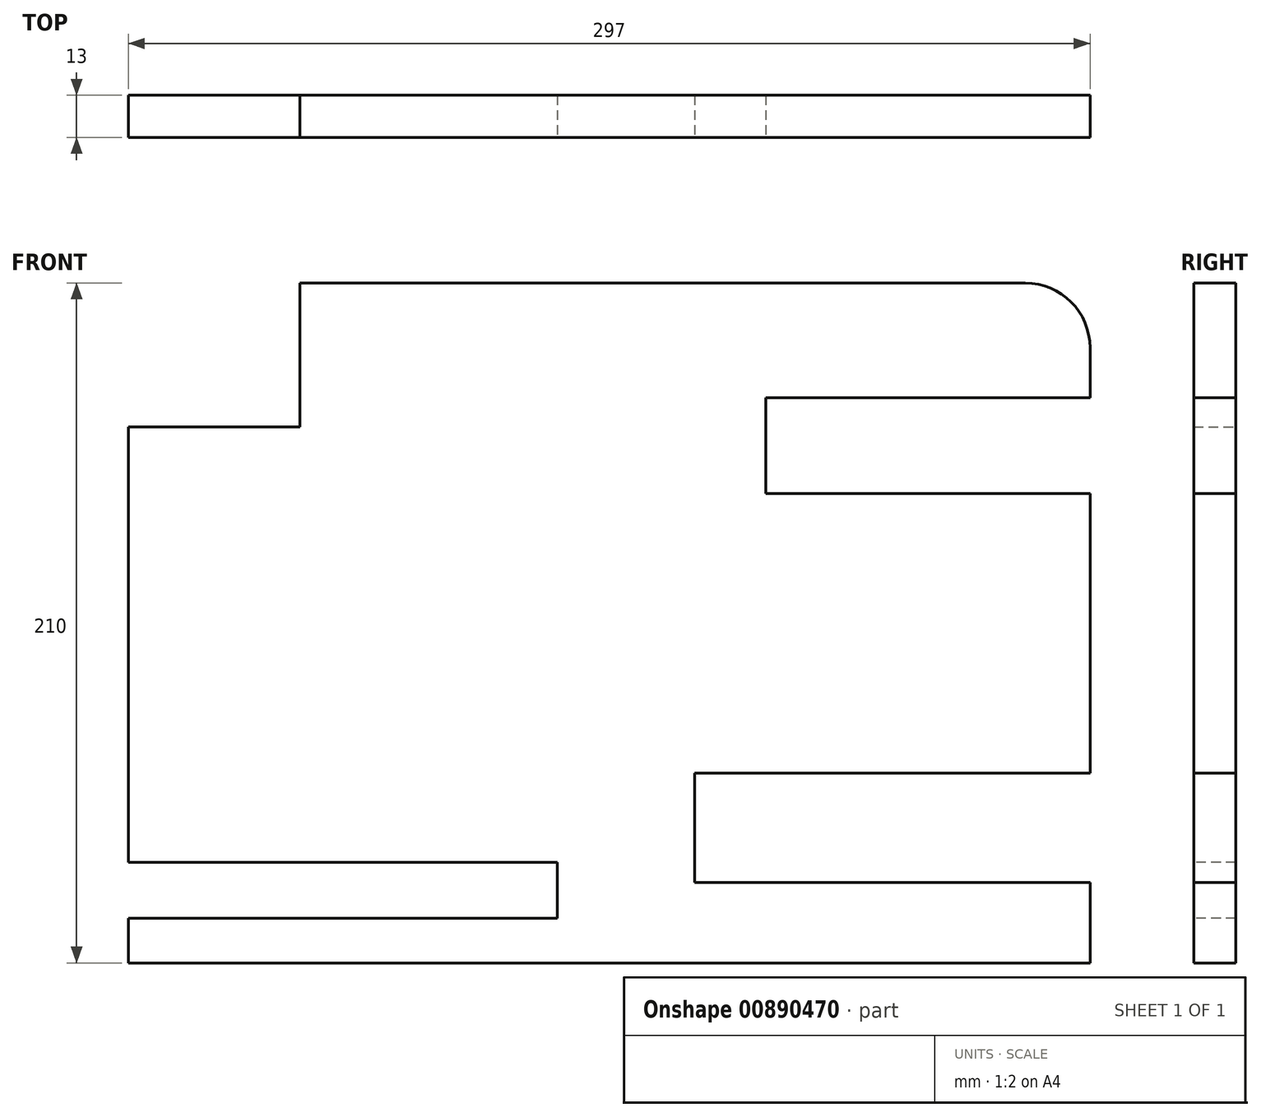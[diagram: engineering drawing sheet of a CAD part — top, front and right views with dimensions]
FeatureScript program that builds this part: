
annotation { "Feature Type Name" : "Feature", "Feature Type Description" : "" }
export const myFeature = defineFeature(function(context is Context, id is Id, definition is map)
    precondition{}
    {
        {
            var Q0;
            Q0=qCreatedBy(makeId("Front.planeOp"),FACE);
            var sketch = newSketch(context, id + "F0", { "sketchPlane" : qUnion([Q0])});
            skLineSegment(sketch, "E0.bottom", {"start": v(-79.44, 101.56) * mm, "end": v(144.58, 101.56) * mm});
            skLineSegment(sketch, "E0.top", {"start": v(-132.42, -108.44) * mm, "end": v(164.58, -108.44) * mm});
            skLineSegment(sketch, "E0.left", {"start": v(-132.42, 57.16) * mm, "end": v(-132.42, -108.44) * mm});
            skLineSegment(sketch, "E0.right", {"start": v(164.58, 81.56) * mm, "end": v(164.58, -108.44) * mm});
            skPoint(sketch, "E1.visualSharp", {"position": v(164.58, 101.56) * mm});
            skArc(sketch, "E1.filletArc", {"start": v(164.58, 81.56) * mm, "mid": v(158.73, 95.7) * mm, "end": v(144.58, 101.56) * mm});
            skLineSegment(sketch, "E2", {"start": v(-79.44, 101.56) * mm, "end": v(-79.44, 57.16) * mm});
            skLineSegment(sketch, "E3", {"start": v(-79.44, 57.16) * mm, "end": v(-132.42, 57.16) * mm});
            skPoint(sketch, "E4.orphan", {"position": v(-132.42, 101.56) * mm});
            skSolve(sketch);
        }
        {
            var Q0;
            Q0 = qSketchRegion(id + "F0", true);
            extrude(context, id + "F1", {"entities" : qUnion([Q0]), "depth" : 13 * mm, "offsetDistance" : 25 * mm});
        }
        {
            var Q0;
            Q0=makeQuery(id+"F1.opExtrude","CAP_FACE",FACE,{"disambiguationData":[OSD([sQuery(id+"F0.wireOp",EDGE,"E0.bottom"),sQuery(id+"F0.wireOp",EDGE,"E0.top"),sQuery(id+"F0.wireOp",EDGE,"E0.left"),sQuery(id+"F0.wireOp",EDGE,"E0.right"),sQuery(id+"F0.wireOp",EDGE,"E1.filletArc"),sQuery(id+"F0.wireOp",EDGE,"E2"),sQuery(id+"F0.wireOp",EDGE,"E3")])],"isStart":false});
            var sketch = newSketch(context, id + "F2", { "sketchPlane" : qUnion([Q0])});
            skLineSegment(sketch, "E5.bottom", {"start": v(-132.42, -77.33) * mm, "end": v(0, -77.33) * mm});
            skLineSegment(sketch, "E5.top", {"start": v(-132.42, -94.6) * mm, "end": v(0, -94.6) * mm});
            skLineSegment(sketch, "E5.left", {"start": v(-132.42, -77.33) * mm, "end": v(-132.42, -94.6) * mm});
            skLineSegment(sketch, "E5.right", {"start": v(0, -77.33) * mm, "end": v(0, -94.6) * mm});
            skSolve(sketch);
        }
        {
            var Q0;
            Q0 = qSketchRegion(id + "F2", true);
            extrude(context, id + "F3", {"entities" : qUnion([Q0]), "operationType" : NewBodyOperationType.REMOVE, "oppositeDirection" : true, "depth" : 13 * mm, "offsetDistance" : 25 * mm});
        }
        {
            var Q0;
            Q0=makeQuery(id+"F1.opExtrude","CAP_FACE",FACE,{"disambiguationData":[OSD([sQuery(id+"F0.wireOp",EDGE,"E0.bottom"),sQuery(id+"F0.wireOp",EDGE,"E0.top"),sQuery(id+"F0.wireOp",EDGE,"E0.left"),sQuery(id+"F0.wireOp",EDGE,"E0.right"),sQuery(id+"F0.wireOp",EDGE,"E1.filletArc"),sQuery(id+"F0.wireOp",EDGE,"E2"),sQuery(id+"F0.wireOp",EDGE,"E3")])],"isStart":false});
            var sketch = newSketch(context, id + "F4", { "sketchPlane" : qUnion([Q0])});
            skLineSegment(sketch, "E6.bottom", {"start": v(164.58, 66.13) * mm, "end": v(64.4, 66.13) * mm});
            skLineSegment(sketch, "E6.top", {"start": v(164.58, 36.57) * mm, "end": v(64.4, 36.57) * mm});
            skLineSegment(sketch, "E6.left", {"start": v(164.58, 66.13) * mm, "end": v(164.58, 36.57) * mm});
            skLineSegment(sketch, "E6.right", {"start": v(64.4, 66.13) * mm, "end": v(64.4, 36.57) * mm});
            skSolve(sketch);
        }
        {
            var Q0;
            Q0=makeQuery(id+"F4.imprint","IMPRINT",FACE,{"disambiguationData":[TD([[makeQuery(id+"F4.imprint","IMPRINT",EDGE,{"derivedFrom":sQuery(id+"F4.wireOp",EDGE,"E6.bottom")}),1.0]])]});
            extrude(context, id + "F5", {"entities" : qUnion([Q0]), "operationType" : NewBodyOperationType.REMOVE, "oppositeDirection" : true, "depth" : 13 * mm, "offsetDistance" : 25 * mm});
        }
        {
            var Q0;
            Q0=makeQuery(id+"F1.opExtrude","CAP_FACE",FACE,{"disambiguationData":[OSD([sQuery(id+"F0.wireOp",EDGE,"E0.bottom"),sQuery(id+"F0.wireOp",EDGE,"E0.top"),sQuery(id+"F0.wireOp",EDGE,"E0.left"),sQuery(id+"F0.wireOp",EDGE,"E0.right"),sQuery(id+"F0.wireOp",EDGE,"E1.filletArc"),sQuery(id+"F0.wireOp",EDGE,"E2"),sQuery(id+"F0.wireOp",EDGE,"E3")])],"isStart":false});
            var sketch = newSketch(context, id + "F6", { "sketchPlane" : qUnion([Q0])});
            skLineSegment(sketch, "E7.bottom", {"start": v(164.58, -83.64) * mm, "end": v(42.48, -83.64) * mm});
            skLineSegment(sketch, "E7.top", {"start": v(164.58, -49.77) * mm, "end": v(42.48, -49.77) * mm});
            skLineSegment(sketch, "E7.left", {"start": v(164.58, -83.64) * mm, "end": v(164.58, -49.77) * mm});
            skLineSegment(sketch, "E7.right", {"start": v(42.48, -83.64) * mm, "end": v(42.48, -49.77) * mm});
            skSolve(sketch);
        }
        {
            var Q0;
            Q0=makeQuery(id+"F6.imprint","IMPRINT",FACE,{"disambiguationData":[TD([[makeQuery(id+"F6.imprint","IMPRINT",EDGE,{"derivedFrom":sQuery(id+"F6.wireOp",EDGE,"E7.bottom")}),-1.0]])]});
            extrude(context, id + "F7", {"entities" : qUnion([Q0]), "operationType" : NewBodyOperationType.REMOVE, "oppositeDirection" : true, "depth" : 13 * mm, "offsetDistance" : 25 * mm});
        }
        {
            var Q0;
            Q0=makeQuery(id+"F1.opExtrude","CAP_FACE",FACE,{"disambiguationData":[OSD([sQuery(id+"F0.wireOp",EDGE,"E0.bottom"),sQuery(id+"F0.wireOp",EDGE,"E0.top"),sQuery(id+"F0.wireOp",EDGE,"E0.left"),sQuery(id+"F0.wireOp",EDGE,"E0.right"),sQuery(id+"F0.wireOp",EDGE,"E1.filletArc"),sQuery(id+"F0.wireOp",EDGE,"E2"),sQuery(id+"F0.wireOp",EDGE,"E3")])],"isStart":false});
            var sketch = newSketch(context, id + "F8", { "sketchPlane" : qUnion([Q0])});
            skCircle(sketch, "E8", {"center": v(-113.5, 2.67) * mm, "radius": 4.5 * mm});
            skCircle(sketch, "E9", {"center": v(-43.5, 2.67) * mm, "radius": 4.5 * mm});
            skSolve(sketch);
        }
        {
            var Q0;
            Q0=sQuery(id+"F8.wireOp",EDGE,"E8");
            var Q1;
            Q1=sQuery(id+"F8.wireOp",EDGE,"E9");
            extrude(context, id + "F9", {"bodyType" : ToolBodyType.SURFACE, "surfaceEntities" : qUnion([Q0, Q1]), "depth" : 15 * mm, "offsetDistance" : 25 * mm});
        }
    });
